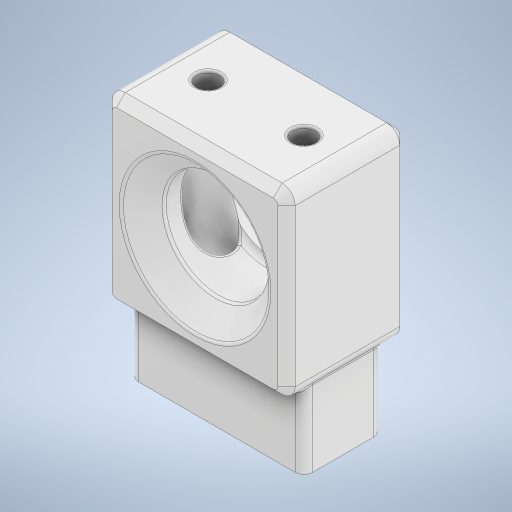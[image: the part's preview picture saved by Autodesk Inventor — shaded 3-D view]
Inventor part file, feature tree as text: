
AUTODESK INVENTOR PART (.ipt)
format: ipt  version: 2024 (Build 280153000, 153)  size: 534,528 bytes
history: native  units: mm
features: fillet x8, sketch x8, extrude x6, plane x3, chamfer x3, projected_geometry x3, hole x2
ambient origin geometry x8: Origin, YZ Plane, XZ Plane, XY Plane, X Axis, Y Axis, Z Axis, Center Point
bodies: Solid1 (feature_tree)
feature tree (33):
  extrude  "Extrusion1"  Depth=42.0mm
  extrude  "Extrusion2"  Depth=31.0mm
  plane  "Work Plane6"
  extrude  "Extrusion9"  TaperAngle=150.0deg  [1 undecoded]
  plane  "Work Plane8"
  extrude  "Extrusion10"  Depth=22.25mm
  chamfer  "Chamfer5"  [1 undecoded]
  chamfer  "Chamfer6"  Distance=2.0mm Angle=45.0deg
  fillet  "Fillet8"  Radius=18.0mm
  chamfer  "Chamfer3"  Distance=14.0mm
  plane  "Work Plane7"
  extrude  "Extrusion8"  Depth=1.0mm
  hole  "Hole4"  [1 undecoded]
  sketch  "Sketch11"  dims[d67=3.0mm d68=2.0mm d69=2.0mm d70=45.0deg d73=18.0mm]
  fillet  "Fillet16"  Radius=18.0mm
  hole  "Hole5"  [1 undecoded]
  fillet  "Fillet17"  Radius=1.0mm
  extrude  "Extrusion11"  Depth=1.0mm TaperAngle=45.0deg
  fillet  "Fillet18"  Radius=22.0mm
  fillet  "Fillet19"  [1 undecoded]
  fillet  "Fillet11"  Radius=7.0mm
  fillet  "Fillet12"  Radius=24.0mm
  fillet  "Fillet20"  [1 undecoded]
  sketch  "Sketch1"  dims[d0=42.0mm d1=42.0mm]
  sketch  "Sketch3"  dims[d2=31.0mm d3=31.0mm]
  sketch  "Sketch9"  dims[d4=19.198622mm d5=150.0deg]
  sketch  "Sketch10"  dims[d6=28.0mm d7=0.0mm d17=22.25mm d18=0.0mm d19=0.0mm]
  projected_geometry  "Projected Loop3"
  projected_geometry  "Projected Loop4"
  sketch  "Sketch12"  dims[d74=40.0mm d75=14.0mm d76=0.0mm]
  sketch  "Sketch14"  dims[d84=5.3mm d85=6.0mm d86=4.0mm d87=2.0mm d88=90.0deg d89=10.0mm d90=0.0mm]
  sketch  "Sketch15"  dims[d91=10.0mm d92=6.0mm d93=4.0mm d94=2.0mm d95=90.0deg d96=40.0mm d97=0.0mm d105=2.0mm d106=1.0mm d114=18.0mm d115=20.0mm d116=0.0mm d117=1.0mm d118=2.0mm d119=60.0deg d120=5.0mm d121=2.0mm d122=45.0deg d124=22.0mm d125=-3.0mm d126=7.0mm d127=24.0mm d128=0.0mm d129=0.0mm d130=2.0mm d131=0.5mm d132=0.0mm d133=0.0mm d134=0.5mm d135=0.5mm d136=1.0mm d137=17.0mm]
  projected_geometry  "Projected Loop5"
note: 6 required parameter values undecoded (feature->parameter linkage not recoverable at this tier; creation-order binding heuristic only, values carry confidence <= 0.55)
